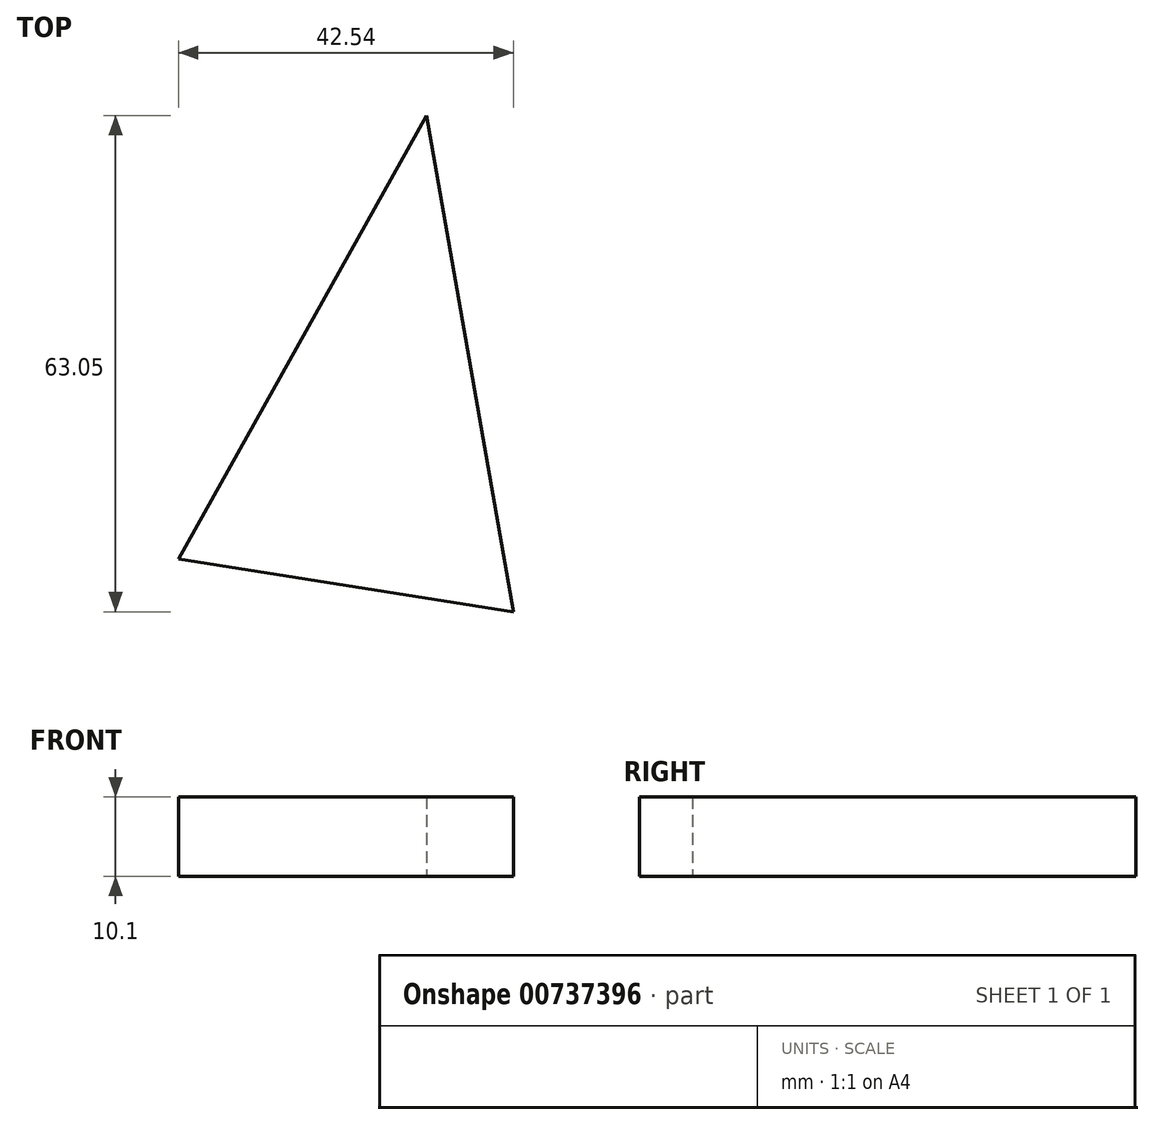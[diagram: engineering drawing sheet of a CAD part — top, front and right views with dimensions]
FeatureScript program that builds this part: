
annotation { "Feature Type Name" : "Feature", "Feature Type Description" : "" }
export const myFeature = defineFeature(function(context is Context, id is Id, definition is map)
    precondition{}
    {
        {
            var Q0;
            Q0=qCreatedBy(makeId("Top.planeOp"),FACE);
            var sketch = newSketch(context, id + "F0", { "sketchPlane" : qUnion([Q0])});
            skLineSegment(sketch, "E0", {"start": v(-65.67, -56.3) * mm, "end": v(-23.13, -63.05) * mm});
            skLineSegment(sketch, "E1", {"start": v(-23.13, -63.05) * mm, "end": v(-34.19, 0) * mm});
            skLineSegment(sketch, "E2", {"start": v(-34.19, 0) * mm, "end": v(-65.67, -56.3) * mm});
            skSolve(sketch);
        }
        {
            var Q0;
            Q0=makeQuery(id+"F0.imprint","IMPRINT",FACE,{"disambiguationData":[TD([[makeQuery(id+"F0.imprint","IMPRINT",EDGE,{"derivedFrom":sQuery(id+"F0.wireOp",EDGE,"E0")}),1.0]])]});
            var sketch = newSketch(context, id + "F1", { "sketchPlane" : qUnion([Q0])});
            skSolve(sketch);
        }
        {
            var Q0;
            Q0=makeQuery(id+"F1.imprint","IMPRINT",FACE,{"disambiguationData":[TD([[makeQuery(id+"F1.imprint","IMPRINT",EDGE,{"derivedFrom":makeQuery(id+"F0.imprint","IMPRINT",EDGE,{"derivedFrom":sQuery(id+"F0.wireOp",EDGE,"E0")})}),1.0]])]});
            extrude(context, id + "F2", {"entities" : qUnion([Q0]), "depth" : 10.1 * mm, "offsetDistance" : 25.4 * mm});
        }
    });
